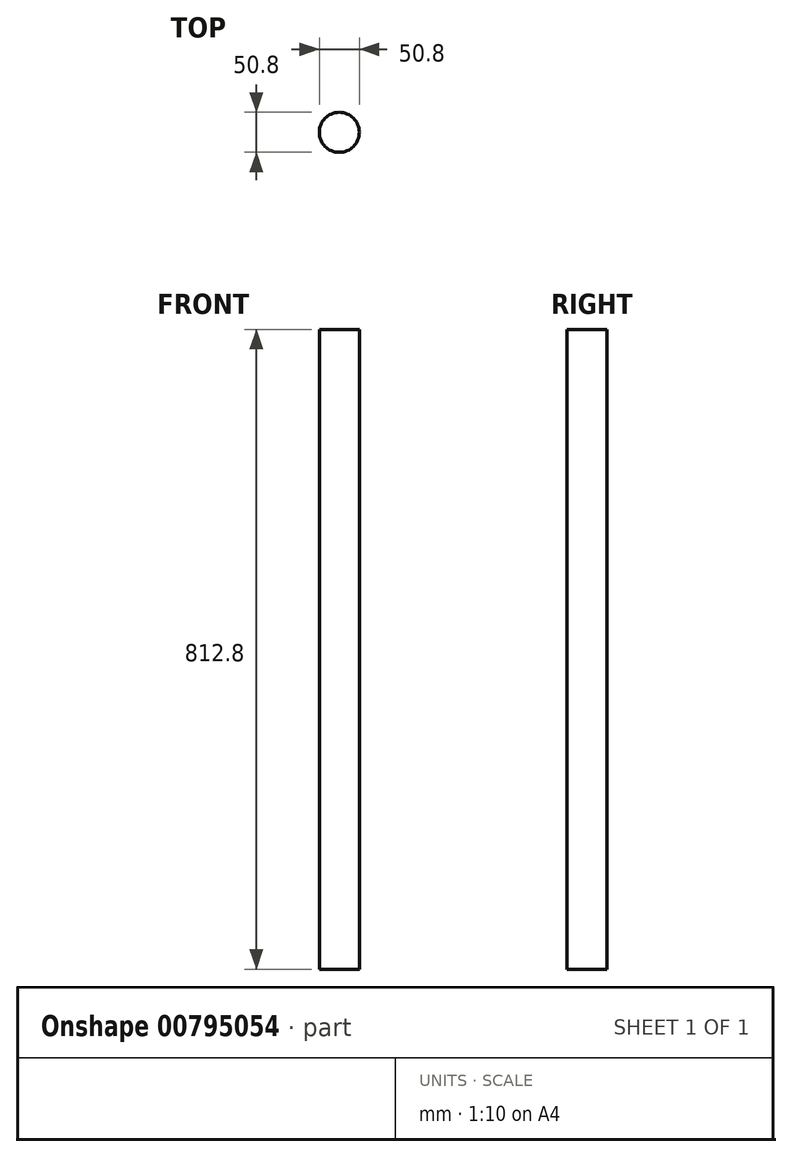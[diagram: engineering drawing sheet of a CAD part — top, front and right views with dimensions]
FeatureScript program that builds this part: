
annotation { "Feature Type Name" : "Feature", "Feature Type Description" : "" }
export const myFeature = defineFeature(function(context is Context, id is Id, definition is map)
    precondition{}
    {
        {
            var Q0;
            Q0=qCreatedBy(makeId("Top.planeOp"),FACE);
            var sketch = newSketch(context, id + "F0", { "sketchPlane" : qUnion([Q0])});
            skCircle(sketch, "E0", {"center": v(0, 0) * mm, "radius": 25.4 * mm});
            skSolve(sketch);
        }
        {
            var Q0;
            Q0=qSketchRegion(id+"F0",true);
            extrude(context, id + "F1", {"entities" : qUnion([Q0]), "depth" : 812.8 * mm, "offsetDistance" : 25.4 * mm});
        }
    });
